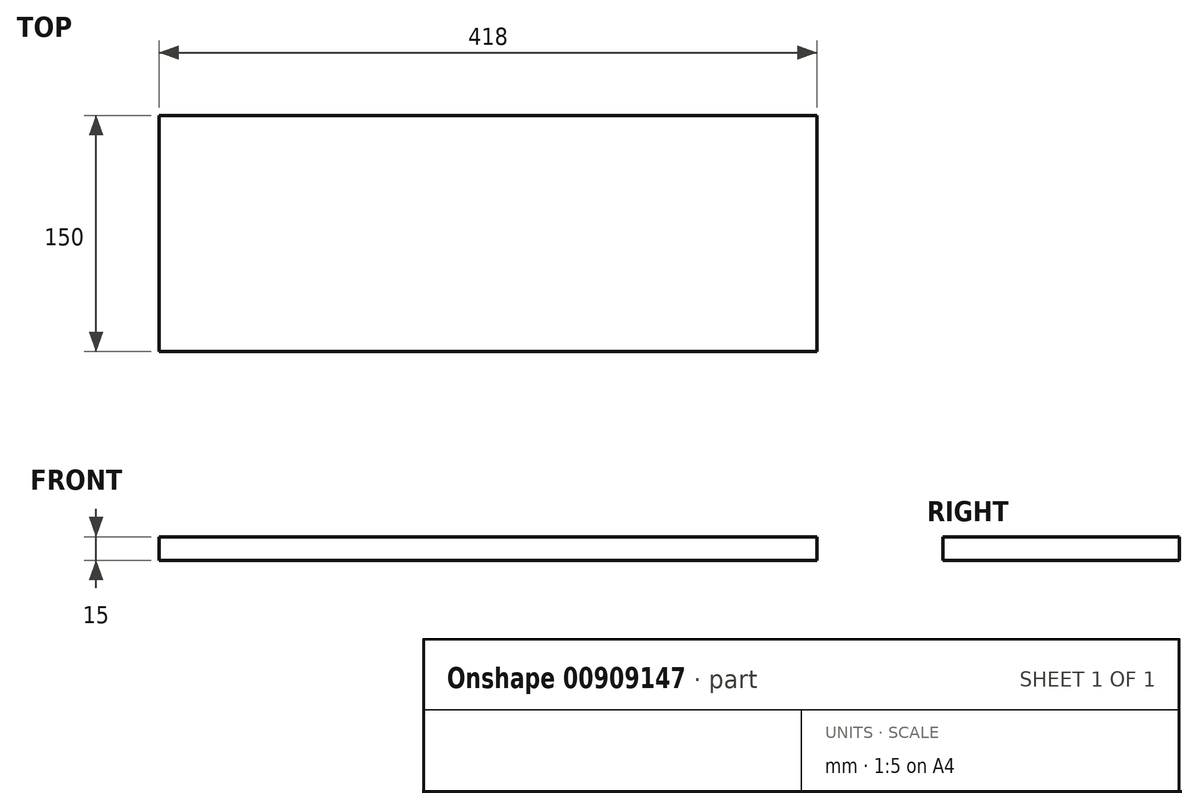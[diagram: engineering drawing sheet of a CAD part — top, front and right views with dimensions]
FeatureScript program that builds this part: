
annotation { "Feature Type Name" : "Feature", "Feature Type Description" : "" }
export const myFeature = defineFeature(function(context is Context, id is Id, definition is map)
    precondition{}
    {
        {
            var Q0;
            Q0=qCreatedBy(makeId("Top.planeOp"),FACE);
            var sketch = newSketch(context, id + "F0", { "sketchPlane" : qUnion([Q0])});
            skLineSegment(sketch, "E0.bottom", {"start": v(209, -75) * mm, "end": v(-209, -75) * mm});
            skLineSegment(sketch, "E0.top", {"start": v(209, 75) * mm, "end": v(-209, 75) * mm});
            skLineSegment(sketch, "E0.left", {"start": v(209, -75) * mm, "end": v(209, 75) * mm});
            skLineSegment(sketch, "E0.right", {"start": v(-209, -75) * mm, "end": v(-209, 75) * mm});
            skPoint(sketch, "E0.middle", {"position": v(0, 0) * mm});
            skSolve(sketch);
        }
        {
            var Q0;
            Q0=makeQuery(id+"F0.imprint","IMPRINT",FACE,{"disambiguationData":[TD([[makeQuery(id+"F0.imprint","IMPRINT",EDGE,{"derivedFrom":sQuery(id+"F0.wireOp",EDGE,"E0.bottom")}),-1.0]])]});
            extrude(context, id + "F1", {"entities" : qUnion([Q0]), "depth" : 15 * mm, "offsetDistance" : 25 * mm});
        }
    });
